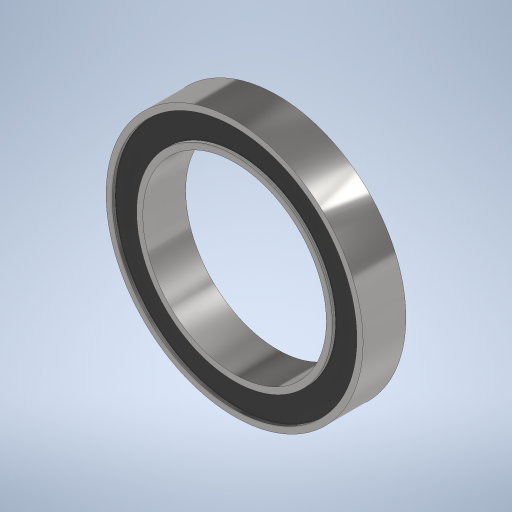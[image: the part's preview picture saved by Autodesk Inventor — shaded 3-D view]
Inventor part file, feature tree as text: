
AUTODESK INVENTOR PART (.ipt)
format: ipt  version: 2023 (Build 270158000, 158)  size: 292,352 bytes
history: native  units: mm
features: extrude x3, sketch x3, projected_geometry x1
ambient origin geometry x8: Origin, YZ Plane, XZ Plane, XY Plane, X Axis, Y Axis, Z Axis, Center Point
bodies: Solid1 (feature_tree)
feature tree (7):
  extrude  "Extrusion1"  Depth=30.0mm
  extrude  "Extrusion2"  Depth=7.0mm
  extrude  "Extrusion3"  Depth=0.5mm TaperAngle=0.0deg
  sketch  "Sketch1"  dims[d0=42.0mm d1=30.0mm]
  sketch  "Sketch2"  dims[d2=7.0mm d3=0.0mm d4=1.0mm]
  projected_geometry  "Projected Loop1"
  sketch  "Sketch3"  dims[d5=1.0mm d6=0.5mm d7=0.0mm d8=0.5mm d9=0.0mm]
